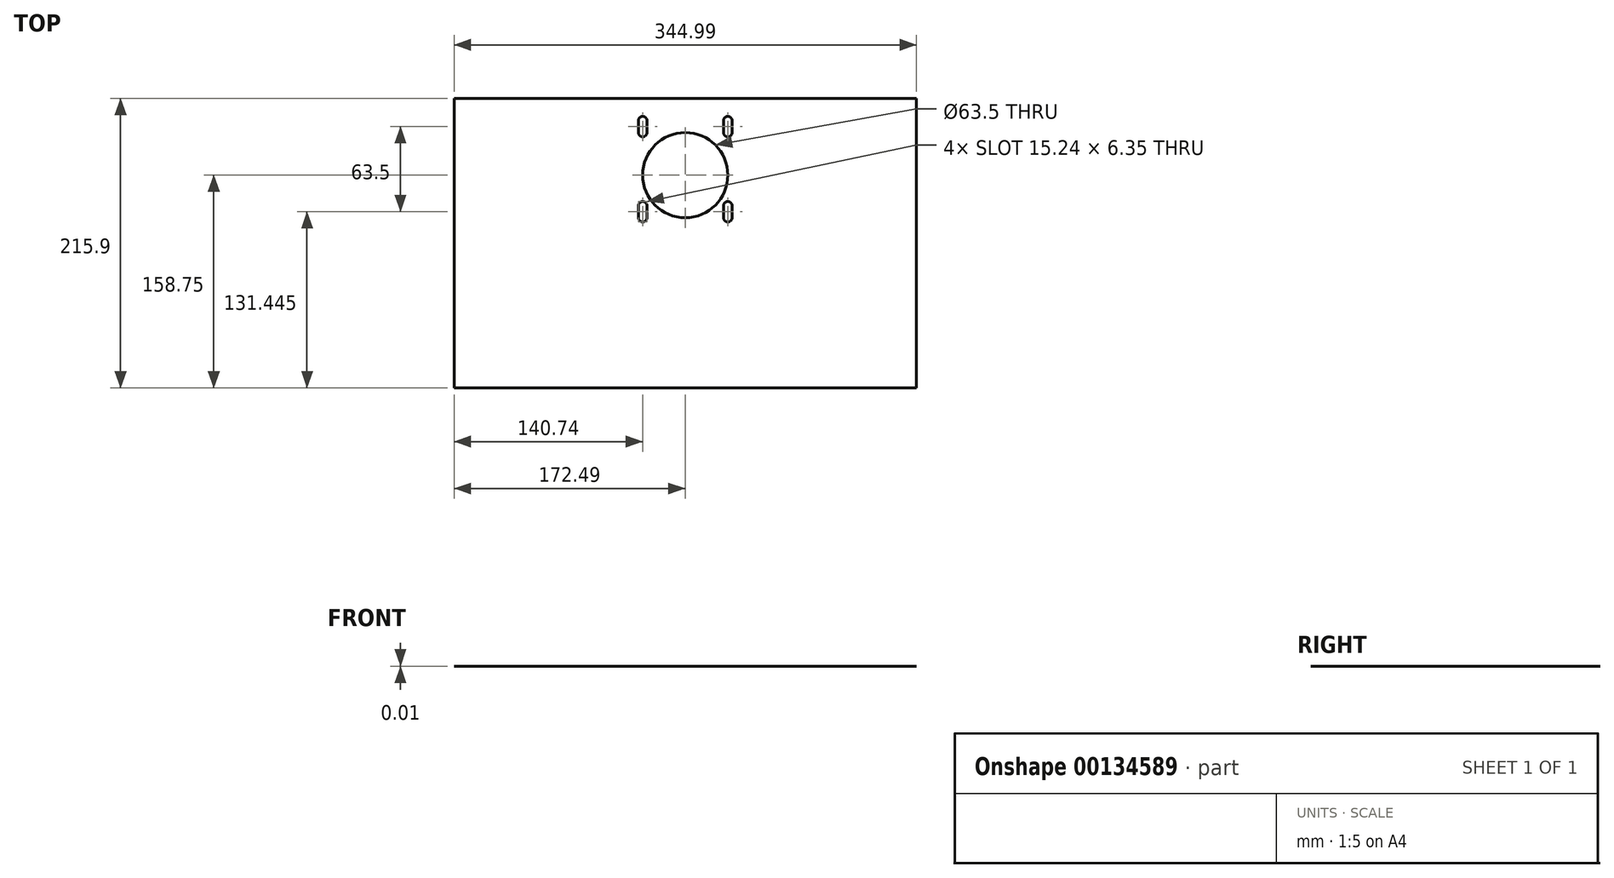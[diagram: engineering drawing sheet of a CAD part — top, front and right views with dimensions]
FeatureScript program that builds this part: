
annotation { "Feature Type Name" : "Feature", "Feature Type Description" : "" }
export const myFeature = defineFeature(function(context is Context, id is Id, definition is map)
    precondition{}
    {
        {
            var Q0;
            Q0=qCreatedBy(makeId("Top.planeOp"),FACE);
            var sketch = newSketch(context, id + "F0", { "sketchPlane" : qUnion([Q0])});
            skLineSegment(sketch, "E0.bottom", {"start": v(-172.5, 57.15) * mm, "end": v(172.5, 57.15) * mm});
            skLineSegment(sketch, "E0.top", {"start": v(-172.5, -158.75) * mm, "end": v(172.5, -158.75) * mm});
            skLineSegment(sketch, "E0.left", {"start": v(-172.5, 57.15) * mm, "end": v(-172.5, -158.75) * mm});
            skLineSegment(sketch, "E0.right", {"start": v(172.5, 57.15) * mm, "end": v(172.5, -158.75) * mm});
            skCircle(sketch, "E1", {"center": v(0, 0) * mm, "radius": 31.75 * mm});
            skCircle(sketch, "E2", {"center": v(-31.75, 31.75) * mm, "radius": 3.17 * mm});
            skCircle(sketch, "E3", {"center": v(-31.75, 40.64) * mm, "radius": 3.18 * mm});
            skLineSegment(sketch, "E4", {"start": v(-28.57, 40.64) * mm, "end": v(-28.57, 31.75) * mm});
            skLineSegment(sketch, "E5", {"start": v(-34.92, 40.6) * mm, "end": v(-34.92, 31.75) * mm});
            skLineSegment(sketch, "E6.0.1.0", {"start": v(-28.57, -22.86) * mm, "end": v(-28.57, -31.75) * mm});
            skLineSegment(sketch, "E6.0.1.1", {"start": v(-34.92, -22.9) * mm, "end": v(-34.92, -31.75) * mm});
            skCircle(sketch, "E6.0.1.2", {"center": v(-31.75, -22.86) * mm, "radius": 3.18 * mm});
            skCircle(sketch, "E6.0.1.3", {"center": v(-31.75, -31.75) * mm, "radius": 3.17 * mm});
            skLineSegment(sketch, "E6.1.0.0", {"start": v(34.92, 40.64) * mm, "end": v(34.92, 31.75) * mm});
            skLineSegment(sketch, "E6.1.0.1", {"start": v(28.58, 40.6) * mm, "end": v(28.58, 31.75) * mm});
            skCircle(sketch, "E6.1.0.2", {"center": v(31.75, 40.64) * mm, "radius": 3.18 * mm});
            skCircle(sketch, "E6.1.0.3", {"center": v(31.75, 31.75) * mm, "radius": 3.17 * mm});
            skLineSegment(sketch, "E6.1.1.0", {"start": v(34.92, -22.86) * mm, "end": v(34.92, -31.75) * mm});
            skLineSegment(sketch, "E6.1.1.1", {"start": v(28.58, -22.9) * mm, "end": v(28.58, -31.75) * mm});
            skCircle(sketch, "E6.1.1.2", {"center": v(31.75, -22.86) * mm, "radius": 3.18 * mm});
            skCircle(sketch, "E6.1.1.3", {"center": v(31.75, -31.75) * mm, "radius": 3.17 * mm});
            skLineSegment(sketch, "E6.direction1", {"start": v(-28.58, 31.75) * mm, "end": v(34.92, 31.75) * mm, "construction": true});
            skLineSegment(sketch, "E6.direction2", {"start": v(-28.57, 31.75) * mm, "end": v(-28.57, -31.75) * mm, "construction": true});
            skSolve(sketch);
        }
        {
            var Q0;
            Q0 = qSketchRegion(id + "F0", true);
            extrude(context, id + "F1", {"entities" : qUnion([Q0]), "depth" : 3 / 203.2 * mm});
        }
    });
